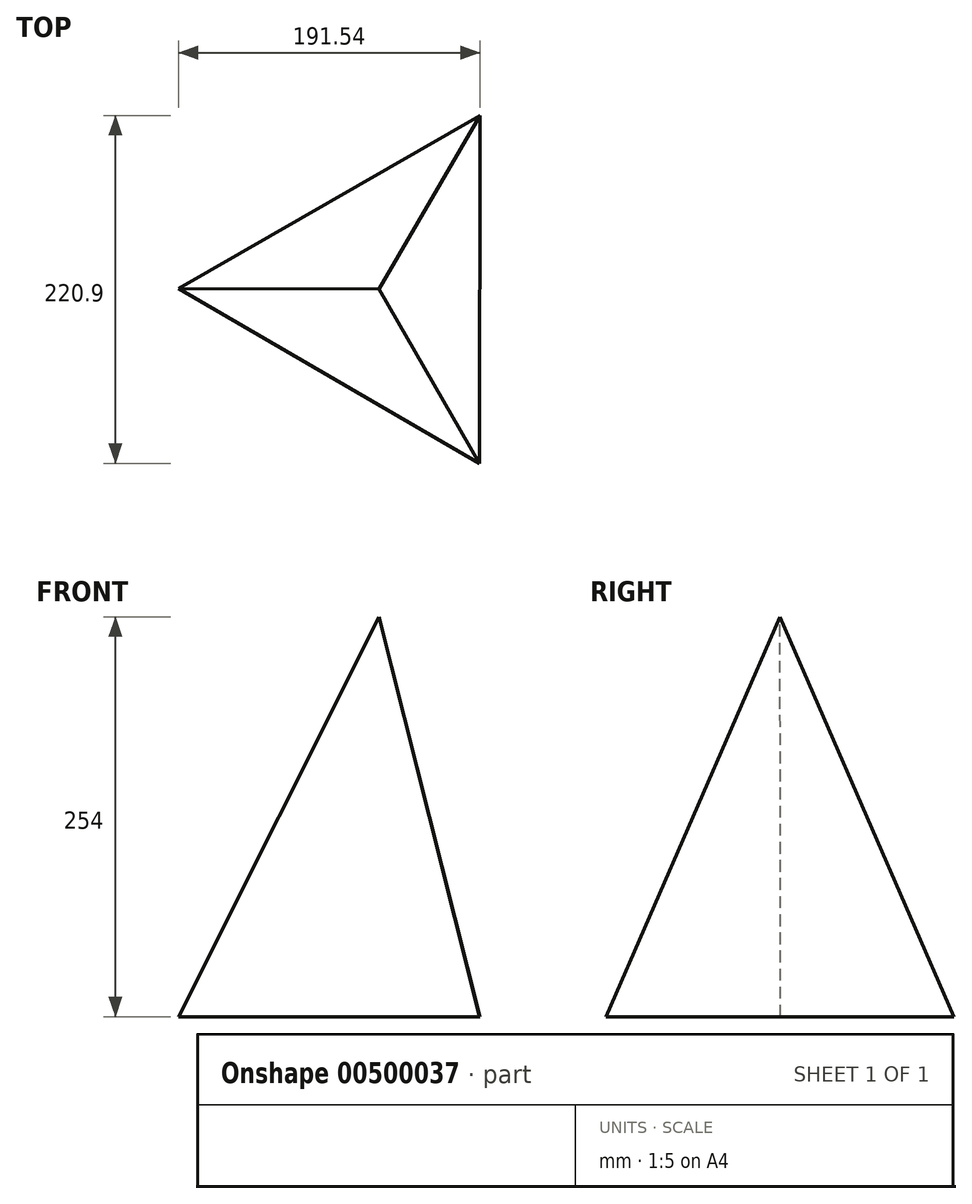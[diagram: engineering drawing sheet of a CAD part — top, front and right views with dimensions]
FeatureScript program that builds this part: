
annotation { "Feature Type Name" : "Feature", "Feature Type Description" : "" }
export const myFeature = defineFeature(function(context is Context, id is Id, definition is map)
    precondition{}
    {
        {
            var Q0;
            Q0=qCreatedBy(makeId("Top.planeOp"),FACE);
            var sketch = newSketch(context, id + "F0", { "sketchPlane" : qUnion([Q0])});
            skCircle(sketch, "E0.cCircle", {"center": v(0, 0) * mm, "radius": 127.54 * mm, "construction": true});
            skLineSegment(sketch, "E0.0", {"start": v(64, 110.3) * mm, "end": v(63.53, -110.59) * mm});
            skLineSegment(sketch, "E0.1", {"start": v(63.53, -110.59) * mm, "end": v(-127.53, 0.28) * mm});
            skLineSegment(sketch, "E0.2", {"start": v(-127.53, 0.28) * mm, "end": v(64, 110.3) * mm});
            skSolve(sketch);
        }
        {
            var Q0;
            Q0=qCreatedBy(makeId("Top.planeOp"),FACE);
            cPlane(context, id + "F1", {"entities" : qUnion([Q0]), "cplaneType" : CPlaneType.OFFSET, "offset" : 254 * mm, "width" : 152.4 * mm, "height" : 152.4 * mm});
        }
        {
            var Q0;
            Q0=qCreatedBy(id+"F1.planeOp",FACE);
            var sketch = newSketch(context, id + "F2", { "sketchPlane" : qUnion([Q0])});
            skPoint(sketch, "E1", {"position": v(0, 0) * mm});
            skSolve(sketch);
        }
        {
            var Q0;
            Q0=makeQuery(id+"F0.imprint","IMPRINT",FACE,{"disambiguationData":[TD([[makeQuery(id+"F0.imprint","IMPRINT",EDGE,{"derivedFrom":sQuery(id+"F0.wireOp",EDGE,"E0.0")}),-1.0]])]});
            var Q1;
            Q1=sQuery(id+"F2.wireOp",VERTEX,"E1");
            loft(context, id + "F3", {"sheetProfilesArray" : [{ "sheetProfileEntities" : qUnion([Q0]) }, { "sheetProfileEntities" : qUnion([Q1]) }]});
        }
    });
